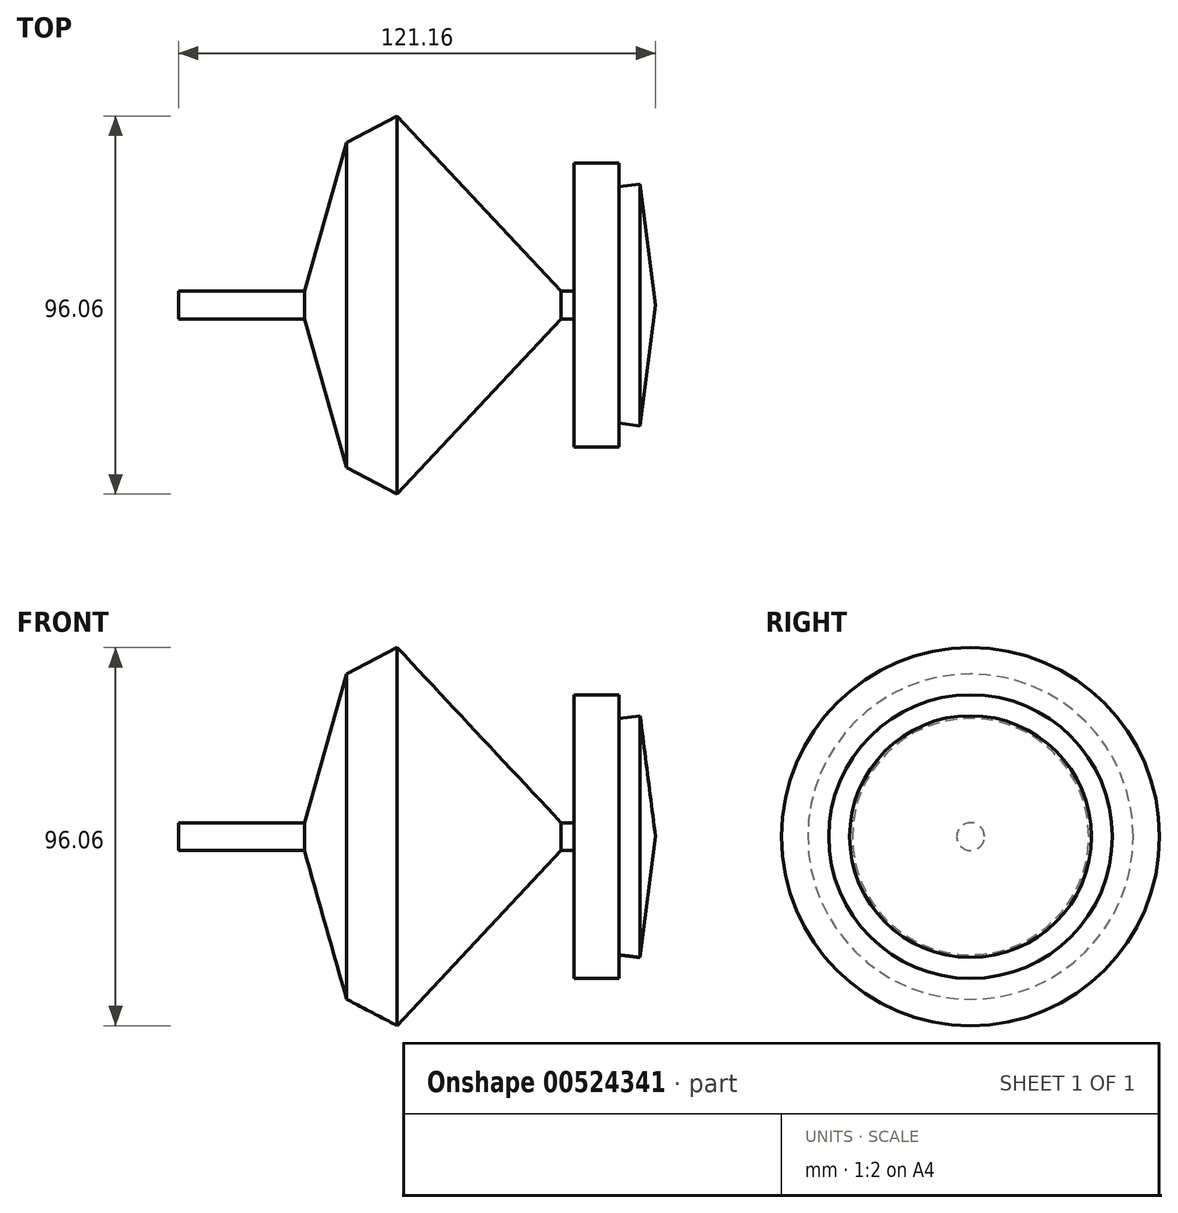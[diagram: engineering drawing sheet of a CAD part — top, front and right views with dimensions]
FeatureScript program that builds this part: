
annotation { "Feature Type Name" : "Feature", "Feature Type Description" : "" }
export const myFeature = defineFeature(function(context is Context, id is Id, definition is map)
    precondition{}
    {
        {
            var Q0;
            Q0=qCreatedBy(makeId("Right.planeOp"),FACE);
            var sketch = newSketch(context, id + "F0", { "sketchPlane" : qUnion([Q0])});
            skCircle(sketch, "E0", {"center": v(0, 0) * mm, "radius": 3.53 * mm});
            skSolve(sketch);
        }
        {
            var Q0;
            Q0 = qSketchRegion(id + "F0", true);
            extrude(context, id + "F1", {"entities" : qUnion([Q0]), "endBound" : BoundingType.SYMMETRIC, "depth" : 120 * mm, "offsetDistance" : 25 * mm});
        }
        {
            var Q0;
            Q0=qCreatedBy(makeId("Front.planeOp"),FACE);
            var sketch = newSketch(context, id + "F2", { "sketchPlane" : qUnion([Q0])});
            skLineSegment(sketch, "E1", {"start": v(-59.48, 0) * mm, "end": v(61.16, 0) * mm});
            skLineSegment(sketch, "E2", {"start": v(61.16, 0) * mm, "end": v(57.25, 30.72) * mm});
            skLineSegment(sketch, "E3", {"start": v(57.25, 30.72) * mm, "end": v(51.85, 30.03) * mm});
            skLineSegment(sketch, "E4", {"start": v(51.85, 36.02) * mm, "end": v(51.85, 30.03) * mm});
            skLineSegment(sketch, "E5", {"start": v(51.85, 36.02) * mm, "end": v(40.5, 36.02) * mm});
            skLineSegment(sketch, "E6", {"start": v(40.5, 36.02) * mm, "end": v(40.5, 0) * mm});
            skLineSegment(sketch, "E7", {"start": v(40.5, 0) * mm, "end": v(-4.47, 48.03) * mm});
            skLineSegment(sketch, "E8", {"start": v(-4.47, 48.03) * mm, "end": v(-17.31, 41.33) * mm});
            skLineSegment(sketch, "E9", {"start": v(-17.31, 41.33) * mm, "end": v(-29.04, 0) * mm});
            skLineSegment(sketch, "E10", {"start": v(-29.04, 0) * mm, "end": v(-56.4, 23.74) * mm});
            skLineSegment(sketch, "E11", {"start": v(-56.4, 23.74) * mm, "end": v(-59.48, 0) * mm});
            skSolve(sketch);
        }
        {
            var Q0;
            {var subQ0=sQuery(id+"F2.wireOp",EDGE,"E7");Q0=makeQuery(id+"F2.imprint","IMPRINT",FACE,{"disambiguationData":[TD([[makeQuery(id+"F2.imprint","IMPRINT",EDGE,{"derivedFrom":subQ0}),1.0]])]});}
            var Q1;
            {var subQ0=sQuery(id+"F2.wireOp",EDGE,"E2");Q1=makeQuery(id+"F2.imprint","IMPRINT",FACE,{"disambiguationData":[TD([[makeQuery(id+"F2.imprint","IMPRINT",EDGE,{"derivedFrom":subQ0}),1.0]])]});}
            var Q2;
            Q2=makeQuery(id+"F1.opExtrude","SWEPT_FACE",FACE,{"disambiguationData":[OSD([sQuery(id+"F0.wireOp",EDGE,"E0")])]});
            revolve(context, id + "F3", {"operationType" : NewBodyOperationType.ADD, "entities" : qUnion([Q0, Q1]), "axis" : qUnion([Q2]), "revolveType" : RevolveType.FULL});
        }
    });
